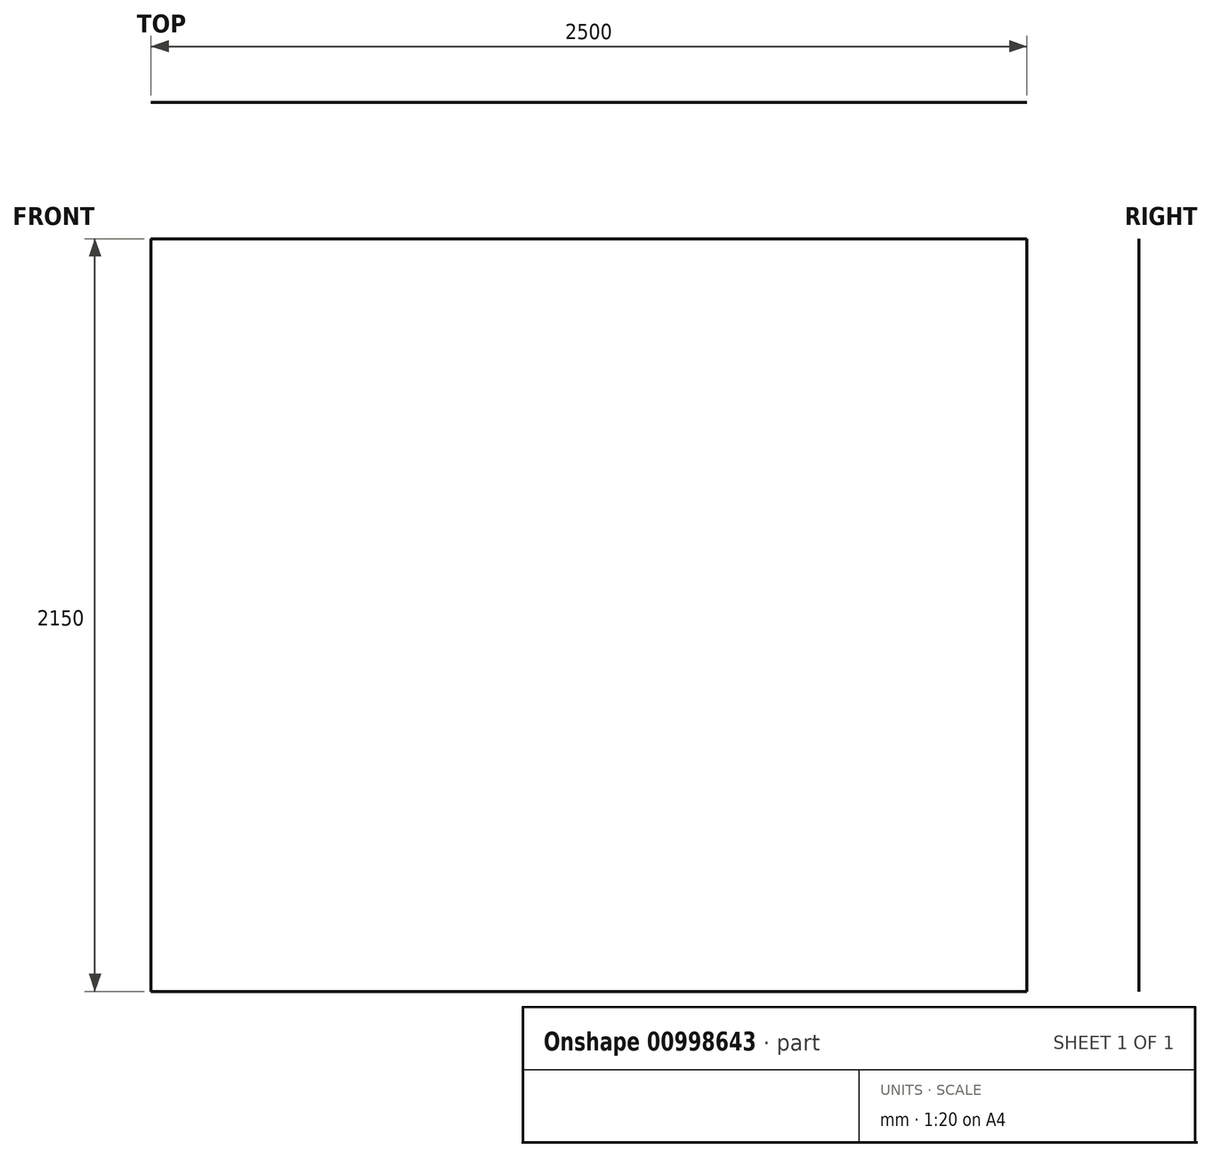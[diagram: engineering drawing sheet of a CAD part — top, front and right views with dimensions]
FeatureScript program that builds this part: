
annotation { "Feature Type Name" : "Feature", "Feature Type Description" : "" }
export const myFeature = defineFeature(function(context is Context, id is Id, definition is map)
    precondition{}
    {
        {
            assignVariable(context, id + "F0", {"name" : "height", "anyValue" : 2150});
        }
        {
            var Q0;
            Q0=qCreatedBy(makeId("Top.planeOp"),FACE);
            var sketch = newSketch(context, id + "F1", { "sketchPlane" : qUnion([Q0])});
            skLineSegment(sketch, "E0.bottom", {"start": v(0, 0) * mm, "end": v(2500, 0) * mm});
            skLineSegment(sketch, "E0.top", {"start": v(0, -2400) * mm, "end": v(2500, -2400) * mm});
            skLineSegment(sketch, "E0.left", {"start": v(0, 0) * mm, "end": v(0, -2400) * mm});
            skLineSegment(sketch, "E0.right", {"start": v(2500, 0) * mm, "end": v(2500, -2400) * mm});
            skSolve(sketch);
        }
        {
            var Q0;
            Q0=sQuery(id+"F1.wireOp",EDGE,"E0.top");
            extrude(context, id + "F2", {"bodyType" : ToolBodyType.SURFACE, "surfaceEntities" : qUnion([Q0]), "depth" : getVariable(context, 'height') * mm, "offsetDistance" : 25 * mm});
        }
    });
